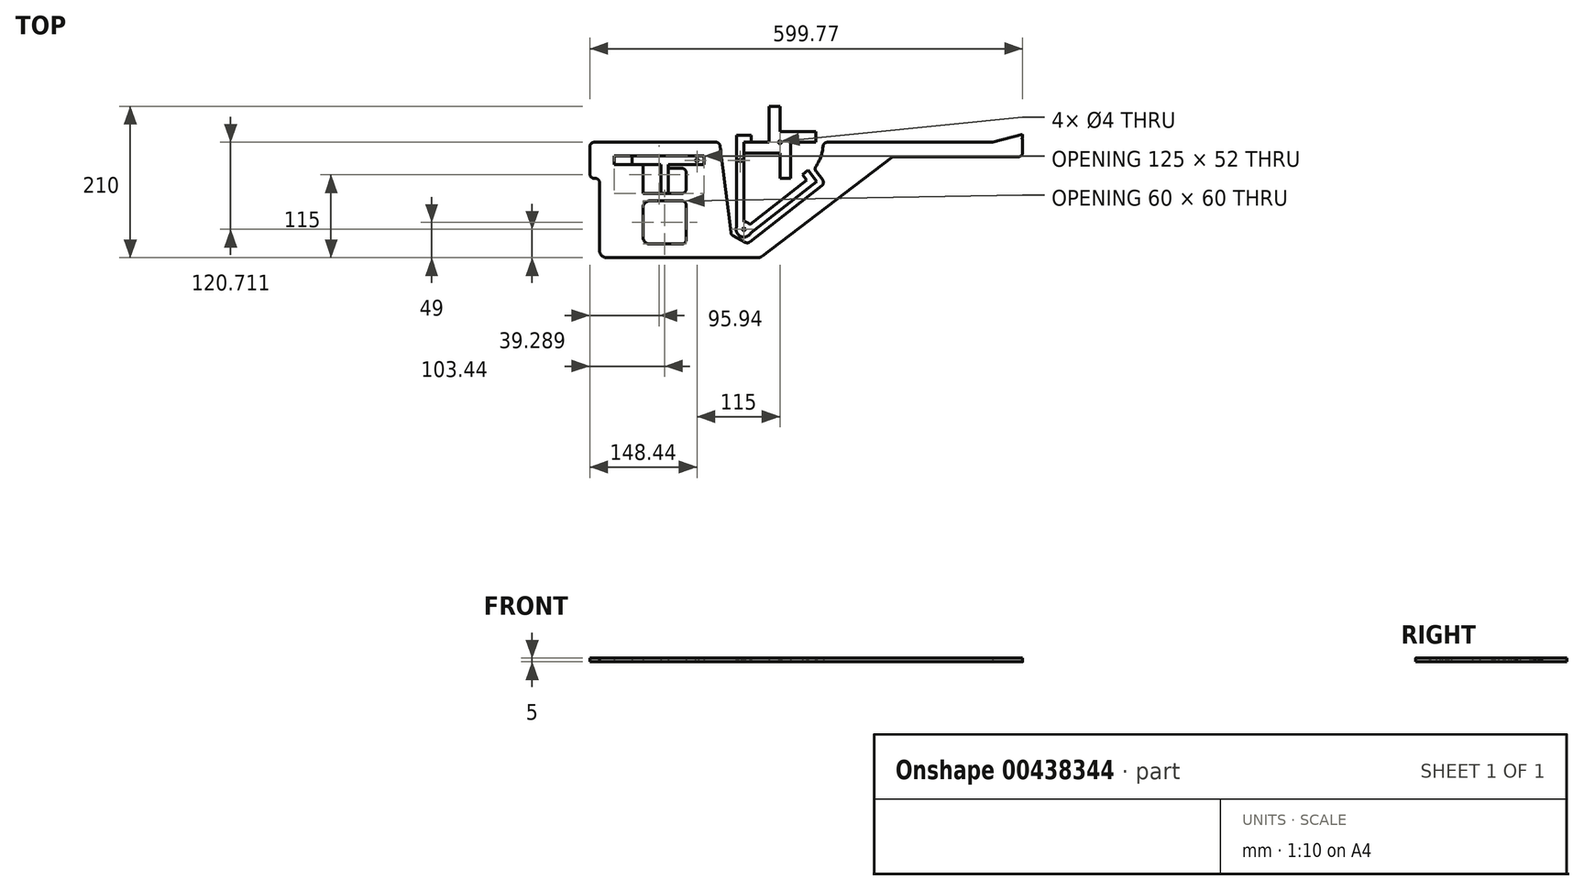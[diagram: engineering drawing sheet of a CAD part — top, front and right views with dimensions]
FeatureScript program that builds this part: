
annotation { "Feature Type Name" : "Feature", "Feature Type Description" : "" }
export const myFeature = defineFeature(function(context is Context, id is Id, definition is map)
    precondition{}
    {
        {
            var Q0;
            Q0=qCreatedBy(makeId("Top.planeOp"),FACE);
            var sketch = newSketch(context, id + "F0", { "sketchPlane" : qUnion([Q0])});
            skPoint(sketch, "E0.middle", {"position": v(0, 0) * mm});
            skLineSegment(sketch, "E1.bottom", {"start": v(0, 0) * mm, "end": v(15, 0) * mm});
            skLineSegment(sketch, "E1.top", {"start": v(0, -50) * mm, "end": v(15, -50) * mm});
            skLineSegment(sketch, "E1.left", {"start": v(0, 0) * mm, "end": v(0, -50) * mm});
            skLineSegment(sketch, "E1.right", {"start": v(15, 0) * mm, "end": v(15, -50) * mm});
            skLineSegment(sketch, "E2.bottom", {"start": v(0, 0) * mm, "end": v(-50, 0) * mm});
            skLineSegment(sketch, "E2.top", {"start": v(0, -15) * mm, "end": v(-50, -15) * mm});
            skLineSegment(sketch, "E2.left", {"start": v(0, 0) * mm, "end": v(0, -15) * mm});
            skLineSegment(sketch, "E2.right", {"start": v(-50, 0) * mm, "end": v(-50, -15) * mm});
            skLineSegment(sketch, "E3.bottom", {"start": v(0, 0) * mm, "end": v(-15, 0) * mm});
            skLineSegment(sketch, "E3.top", {"start": v(0, 50) * mm, "end": v(-15, 50) * mm});
            skLineSegment(sketch, "E3.left", {"start": v(0, 0) * mm, "end": v(0, 50) * mm});
            skLineSegment(sketch, "E3.right", {"start": v(-15, 0) * mm, "end": v(-15, 50) * mm});
            skLineSegment(sketch, "E4.bottom", {"start": v(0, 0) * mm, "end": v(50, 0) * mm});
            skLineSegment(sketch, "E4.top", {"start": v(0, 15) * mm, "end": v(50, 15) * mm});
            skLineSegment(sketch, "E4.left", {"start": v(0, 0) * mm, "end": v(0, 15) * mm});
            skLineSegment(sketch, "E4.right", {"start": v(50, 0) * mm, "end": v(50, 15) * mm});
            skCircle(sketch, "E5", {"center": v(0, 0) * mm, "radius": 2 * mm});
            skSolve(sketch);
        }
        {
            var Q0;
            Q0 = qSketchRegion(id + "F0", true);
            extrude(context, id + "F1", {"entities" : qUnion([Q0]), "depth" : 5 * mm});
        }
        {
            var Q0;
            Q0=qCreatedBy(makeId("Top.planeOp"),FACE);
            var sketch = newSketch(context, id + "F2", { "sketchPlane" : qUnion([Q0])});
            skLineSegment(sketch, "E6", {"start": v(-50, 0) * mm, "end": v(-40, 0) * mm});
            skLineSegment(sketch, "E7", {"start": v(-40, 0) * mm, "end": v(-40, 10) * mm});
            skLineSegment(sketch, "E8", {"start": v(-40, 10) * mm, "end": v(-60, 10) * mm});
            skLineSegment(sketch, "E9", {"start": v(45.12, -46.4) * mm, "end": v(38.96, -38.51) * mm});
            skLineSegment(sketch, "E10", {"start": v(38.96, -38.51) * mm, "end": v(31.08, -44.67) * mm});
            skLineSegment(sketch, "E11", {"start": v(31.08, -44.67) * mm, "end": v(37.24, -52.55) * mm});
            skLineSegment(sketch, "E12", {"start": v(45.12, -46.4) * mm, "end": v(51.28, -54.27) * mm});
            skPoint(sketch, "E13", {"position": v(-50, -120.71) * mm});
            skCircle(sketch, "E14", {"center": v(-50, -120.71) * mm, "radius": 10.71 * mm});
            skLineSegment(sketch, "E15", {"start": v(-50, 0) * mm, "end": v(-50, -110) * mm});
            skLineSegment(sketch, "E16", {"start": v(-60, 10) * mm, "end": v(-60, -116.87) * mm});
            skLineSegment(sketch, "E17", {"start": v(37.24, -52.55) * mm, "end": v(-41.56, -114.12) * mm});
            skLineSegment(sketch, "E18", {"start": v(51.28, -54.27) * mm, "end": v(-40.82, -126.23) * mm});
            skCircle(sketch, "E19", {"center": v(-50, -120.71) * mm, "radius": 2 * mm});
            skSolve(sketch);
        }
        {
            var Q0;
            Q0 = qSketchRegion(id + "F2", true);
            extrude(context, id + "F3", {"entities" : qUnion([Q0]), "depth" : 5 * mm});
        }
        {
            var Q0;
            Q0=makeQuery(id+"F3.opExtrude","CAP_FACE",FACE,{"disambiguationData":[OSD([sQuery(id+"F2.wireOp",EDGE,"E6"),sQuery(id+"F2.wireOp",EDGE,"E7"),sQuery(id+"F2.wireOp",EDGE,"E8"),sQuery(id+"F2.wireOp",EDGE,"E9"),sQuery(id+"F2.wireOp",EDGE,"E10"),sQuery(id+"F2.wireOp",EDGE,"E11"),sQuery(id+"F2.wireOp",EDGE,"E12"),sQuery(id+"F2.wireOp",EDGE,"E14"),sQuery(id+"F2.wireOp",EDGE,"E15"),sQuery(id+"F2.wireOp",EDGE,"E16"),sQuery(id+"F2.wireOp",EDGE,"E17"),sQuery(id+"F2.wireOp",EDGE,"E18")])],"isStart":false});
            var sketch = newSketch(context, id + "F4", { "sketchPlane" : qUnion([Q0])});
            skPoint(sketch, "E20", {"position": v(-55, -25) * mm});
            skCircle(sketch, "E21", {"center": v(-55, -25) * mm, "radius": 2 * mm});
            skSolve(sketch);
        }
        {
            var Q0;
            Q0=makeQuery(id+"F4.imprint","IMPRINT",FACE,{"disambiguationData":[TD([[makeQuery(id+"F4.imprint","IMPRINT",EDGE,{"derivedFrom":sQuery(id+"F4.wireOp",EDGE,"E21")}),1.0]])]});
            extrude(context, id + "F5", {"entities" : qUnion([Q0]), "operationType" : NewBodyOperationType.REMOVE, "endBound" : BoundingType.THROUGH_ALL, "oppositeDirection" : true, "depth" : 25 * mm});
        }
        {
            var Q0;
            Q0=qCreatedBy(makeId("Top.planeOp"),FACE);
            var sketch = newSketch(context, id + "F6", { "sketchPlane" : qUnion([Q0])});
            skPoint(sketch, "E22", {"position": v(-55, -25) * mm});
            skPoint(sketch, "E23", {"position": v(-115, -25) * mm});
            skLineSegment(sketch, "E24", {"start": v(-155, -31) * mm, "end": v(-155, -71) * mm});
            skLineSegment(sketch, "E25", {"start": v(-155, -71) * mm, "end": v(-165, -71) * mm});
            skLineSegment(sketch, "E26", {"start": v(-165, -71) * mm, "end": v(-165, -31) * mm});
            skLineSegment(sketch, "E27", {"start": v(-165, -31) * mm, "end": v(-205, -31) * mm});
            skLineSegment(sketch, "E28", {"start": v(-205, -31) * mm, "end": v(-205, -19) * mm});
            skLineSegment(sketch, "E29", {"start": v(-205, -19) * mm, "end": v(-105, -19) * mm});
            skLineSegment(sketch, "E30", {"start": v(-155, -31) * mm, "end": v(-105, -31) * mm});
            skLineSegment(sketch, "E31", {"start": v(-105, -31) * mm, "end": v(-105, -19) * mm});
            skCircle(sketch, "E32", {"center": v(-115, -25) * mm, "radius": 2 * mm});
            skSolve(sketch);
        }
        {
            var Q0;
            Q0 = qSketchRegion(id + "F6", true);
            extrude(context, id + "F7", {"entities" : qUnion([Q0]), "depth" : 5 * mm});
        }
        {
            var Q0;
            Q0=qCreatedBy(makeId("Top.planeOp"),FACE);
            var sketch = newSketch(context, id + "F8", { "sketchPlane" : qUnion([Q0])});
            skLineSegment(sketch, "E33", {"start": v(-105, -19) * mm, "end": v(-105, -31) * mm});
            skLineSegment(sketch, "E34", {"start": v(-105, -19) * mm, "end": v(-230, -19) * mm});
            skLineSegment(sketch, "E35", {"start": v(-105, -31) * mm, "end": v(-155, -31) * mm});
            skLineSegment(sketch, "E36", {"start": v(-155, -31) * mm, "end": v(-155, -36) * mm});
            skLineSegment(sketch, "E37", {"start": v(-155, -36) * mm, "end": v(-136, -36) * mm});
            skLineSegment(sketch, "E38", {"start": v(-230, -19) * mm, "end": v(-230, -31) * mm});
            skLineSegment(sketch, "E39", {"start": v(-230, -31) * mm, "end": v(-190, -31) * mm});
            skLineSegment(sketch, "E40", {"start": v(-190, -31) * mm, "end": v(-190, -71) * mm});
            skLineSegment(sketch, "E41", {"start": v(-190, -71) * mm, "end": v(-136, -71) * mm});
            skLineSegment(sketch, "E42", {"start": v(-130, -42) * mm, "end": v(-130, -65) * mm});
            skLineSegment(sketch, "E43", {"start": v(336.33, 4.99) * mm, "end": v(335.33, 4.99) * mm});
            skLineSegment(sketch, "E44", {"start": v(335.33, 4.99) * mm, "end": v(335.33, 5.99) * mm});
            skLineSegment(sketch, "E45", {"start": v(335.33, 5.99) * mm, "end": v(336.33, 5.99) * mm});
            skLineSegment(sketch, "E46", {"start": v(336.33, 5.99) * mm, "end": v(336.33, 10.99) * mm});
            skPoint(sketch, "E47", {"position": v(295, -0.01) * mm});
            skLineSegment(sketch, "E48", {"start": v(295, -0.01) * mm, "end": v(336.33, 10.99) * mm});
            skLineSegment(sketch, "E49", {"start": v(336.33, 4.99) * mm, "end": v(336.33, -14.01) * mm});
            skLineSegment(sketch, "E50", {"start": v(330.33, -20.01) * mm, "end": v(158.36, -20.01) * mm});
            skLineSegment(sketch, "E51", {"start": v(295, -0.01) * mm, "end": v(65.73, -0.01) * mm});
            skArc(sketch, "E52", {"start": v(59.75, -5.47) * mm, "mid": v(56.53, -20.11) * mm, "end": v(49.77, -33.5) * mm});
            skLineSegment(sketch, "E53", {"start": v(50.02, -40.55) * mm, "end": v(58.94, -51.96) * mm});
            skLineSegment(sketch, "E54", {"start": v(-64.94, -129.61) * mm, "end": v(-47.98, -138.6) * mm});
            skLineSegment(sketch, "E55", {"start": v(-82.8, -5.27) * mm, "end": v(-68.1, -125.04) * mm});
            skLineSegment(sketch, "E56", {"start": v(-41.48, -138.03) * mm, "end": v(57.9, -60.38) * mm});
            skLineSegment(sketch, "E57", {"start": v(-24.61, -157.95) * mm, "end": v(154.72, -21.24) * mm});
            skLineSegment(sketch, "E58", {"start": v(-240, -160) * mm, "end": v(-30.67, -160) * mm});
            skPoint(sketch, "E59.visualSharp", {"position": v(-263.44, 0) * mm});
            skPoint(sketch, "E60.visualSharp", {"position": v(-27.3, -160) * mm});
            skArc(sketch, "E60.filletArc", {"start": v(-30.67, -160) * mm, "mid": v(-27.47, -159.47) * mm, "end": v(-24.61, -157.95) * mm});
            skPoint(sketch, "E61.visualSharp", {"position": v(-83.44, 0) * mm});
            skArc(sketch, "E61.filletArc", {"start": v(-82.8, -5.27) * mm, "mid": v(-84.78, -1.5) * mm, "end": v(-88.75, 0) * mm});
            skPoint(sketch, "E62.visualSharp", {"position": v(-67.7, -128.15) * mm});
            skArc(sketch, "E62.filletArc", {"start": v(-68.1, -125.04) * mm, "mid": v(-67.08, -127.71) * mm, "end": v(-64.94, -129.61) * mm});
            skPoint(sketch, "E63.visualSharp", {"position": v(-44.55, -140.42) * mm});
            skArc(sketch, "E63.filletArc", {"start": v(-47.98, -138.6) * mm, "mid": v(-44.65, -139.27) * mm, "end": v(-41.48, -138.03) * mm});
            skPoint(sketch, "E64.visualSharp", {"position": v(62.63, -56.69) * mm});
            skArc(sketch, "E64.filletArc", {"start": v(57.9, -60.38) * mm, "mid": v(60.17, -56.39) * mm, "end": v(58.94, -51.96) * mm});
            skPoint(sketch, "E65.visualSharp", {"position": v(47.24, -36.99) * mm});
            skArc(sketch, "E65.filletArc", {"start": v(49.77, -33.5) * mm, "mid": v(48.75, -37.07) * mm, "end": v(50.02, -40.55) * mm});
            skPoint(sketch, "E66.visualSharp", {"position": v(60, -0.01) * mm});
            skArc(sketch, "E66.filletArc", {"start": v(65.73, -0.01) * mm, "mid": v(61.68, -1.58) * mm, "end": v(59.75, -5.47) * mm});
            skPoint(sketch, "E67.visualSharp", {"position": v(156.33, -20.01) * mm});
            skArc(sketch, "E67.filletArc", {"start": v(158.36, -20.01) * mm, "mid": v(156.44, -20.33) * mm, "end": v(154.72, -21.24) * mm});
            skPoint(sketch, "E68.visualSharp", {"position": v(336.33, -20.01) * mm});
            skArc(sketch, "E68.filletArc", {"start": v(330.33, -20.01) * mm, "mid": v(334.57, -18.26) * mm, "end": v(336.33, -14.01) * mm});
            skLineSegment(sketch, "E69", {"start": v(-136, -81) * mm, "end": v(-180, -81) * mm});
            skLineSegment(sketch, "E70", {"start": v(-190, -91) * mm, "end": v(-190, -131) * mm});
            skLineSegment(sketch, "E71", {"start": v(-180, -141) * mm, "end": v(-136, -141) * mm});
            skLineSegment(sketch, "E72", {"start": v(-130, -87) * mm, "end": v(-130, -135) * mm});
            skLineSegment(sketch, "E73", {"start": v(-250, -150) * mm, "end": v(-250, -56) * mm});
            skLineSegment(sketch, "E74", {"start": v(-257.44, 0) * mm, "end": v(-88.75, 0) * mm});
            skArc(sketch, "E75.filletArc", {"start": v(-257.44, 0) * mm, "mid": v(-261.69, -1.76) * mm, "end": v(-263.44, -6) * mm});
            skPoint(sketch, "E76.visualSharp", {"position": v(-250, -160) * mm});
            skArc(sketch, "E76.filletArc", {"start": v(-250, -150) * mm, "mid": v(-247.07, -157.07) * mm, "end": v(-240, -160) * mm});
            skLineSegment(sketch, "E77", {"start": v(-263.44, -6) * mm, "end": v(-263.44, -44) * mm});
            skLineSegment(sketch, "E78", {"start": v(-257.44, -50) * mm, "end": v(-256, -50) * mm});
            skPoint(sketch, "E79.visualSharp", {"position": v(-250, -50) * mm});
            skArc(sketch, "E79.filletArc", {"start": v(-250, -56) * mm, "mid": v(-251.76, -51.76) * mm, "end": v(-256, -50) * mm});
            skPoint(sketch, "E80.visualSharp", {"position": v(-263.44, -50) * mm});
            skArc(sketch, "E80.filletArc", {"start": v(-263.44, -44) * mm, "mid": v(-261.69, -48.24) * mm, "end": v(-257.44, -50) * mm});
            skPoint(sketch, "E81.visualSharp", {"position": v(-190, -81) * mm});
            skArc(sketch, "E81.filletArc", {"start": v(-180, -81) * mm, "mid": v(-187.07, -83.93) * mm, "end": v(-190, -91) * mm});
            skPoint(sketch, "E82.visualSharp", {"position": v(-190, -141) * mm});
            skArc(sketch, "E82.filletArc", {"start": v(-190, -131) * mm, "mid": v(-187.07, -138.07) * mm, "end": v(-180, -141) * mm});
            skPoint(sketch, "E83.visualSharp", {"position": v(-130, -81) * mm});
            skArc(sketch, "E83.filletArc", {"start": v(-130, -87) * mm, "mid": v(-131.76, -82.76) * mm, "end": v(-136, -81) * mm});
            skPoint(sketch, "E84.visualSharp", {"position": v(-130, -141) * mm});
            skArc(sketch, "E84.filletArc", {"start": v(-136, -141) * mm, "mid": v(-131.76, -139.24) * mm, "end": v(-130, -135) * mm});
            skPoint(sketch, "E85.visualSharp", {"position": v(-130, -36) * mm});
            skArc(sketch, "E85.filletArc", {"start": v(-130, -42) * mm, "mid": v(-131.76, -37.76) * mm, "end": v(-136, -36) * mm});
            skPoint(sketch, "E86.visualSharp", {"position": v(-130, -71) * mm});
            skArc(sketch, "E86.filletArc", {"start": v(-136, -71) * mm, "mid": v(-131.76, -69.24) * mm, "end": v(-130, -65) * mm});
            skSolve(sketch);
        }
        {
            var Q0;
            Q0 = qSketchRegion(id + "F8", true);
            extrude(context, id + "F9", {"entities" : qUnion([Q0]), "depth" : 5 * mm});
        }
    });
